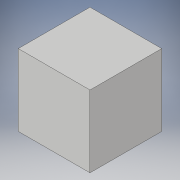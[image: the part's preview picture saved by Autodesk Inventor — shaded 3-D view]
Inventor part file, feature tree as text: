
AUTODESK INVENTOR PART (.ipt)
format: ipt  version: 2019 (Build 230136000, 136)  size: 84,480 bytes
history: native  units: mm
features: extrude x1, sketch x1
ambient origin geometry x8: Origin, YZ Plane, XZ Plane, XY Plane, X Axis, Y Axis, Z Axis, Center Point
bodies: Solid1 (feature_tree)
feature tree (2):
  extrude  "Extrusion1"  Depth=196.0mm
  sketch  "Sketch1"  dims[d0=196.0mm d1=196.0mm d2=196.0mm d3=0.0mm]
